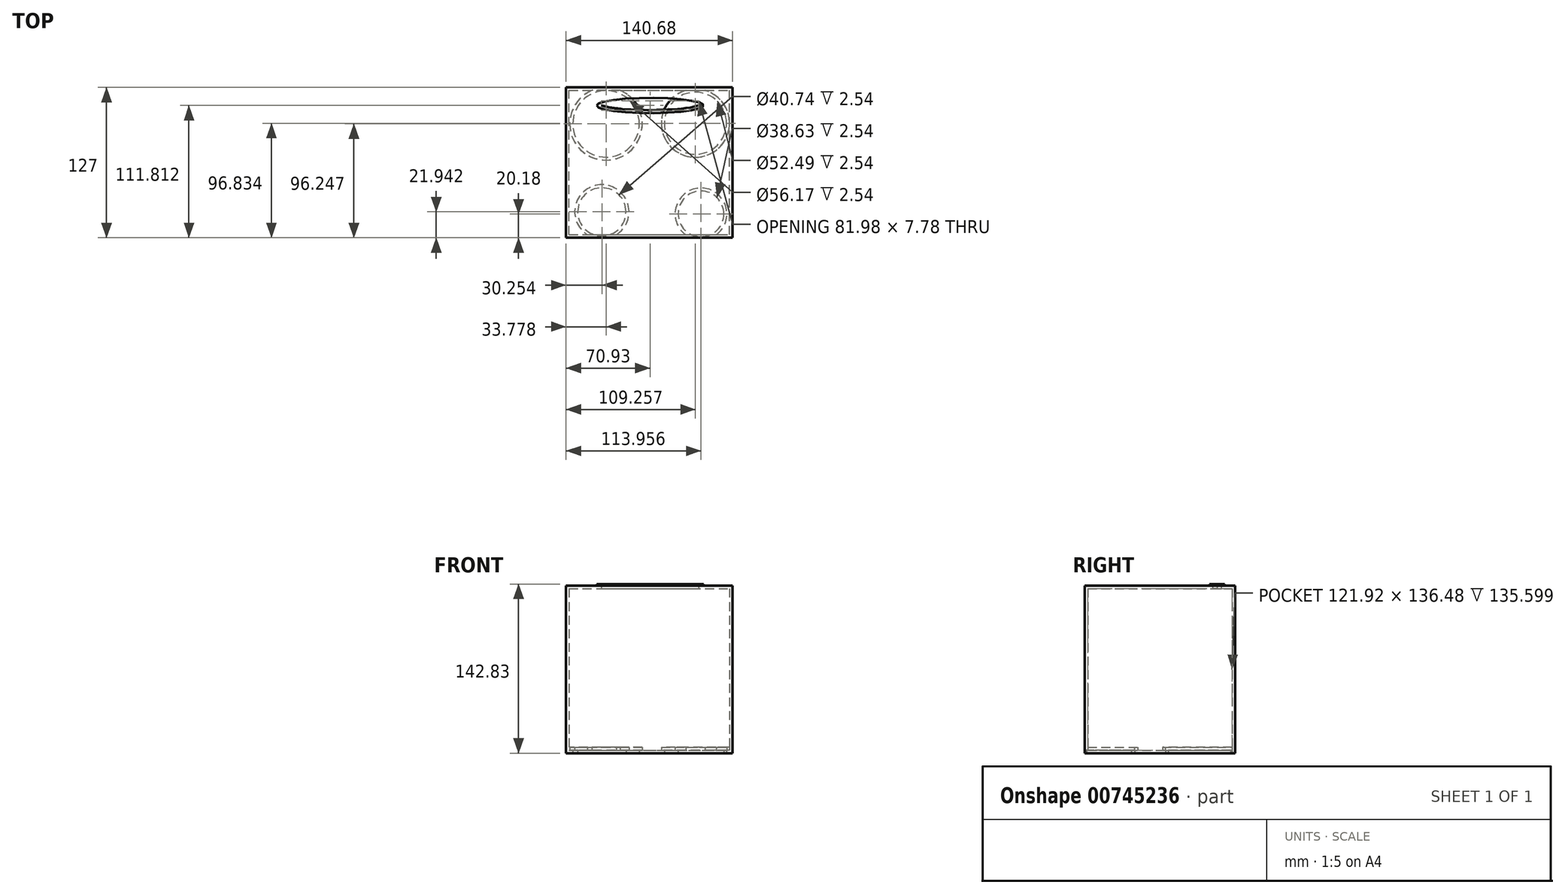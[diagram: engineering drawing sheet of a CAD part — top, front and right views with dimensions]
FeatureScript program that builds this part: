
annotation { "Feature Type Name" : "Feature", "Feature Type Description" : "" }
export const myFeature = defineFeature(function(context is Context, id is Id, definition is map)
    precondition{}
    {
        {
            var Q0;
            Q0=qCreatedBy(makeId("Front.planeOp"),FACE);
            var sketch = newSketch(context, id + "F0", { "sketchPlane" : qUnion([Q0])});
            skLineSegment(sketch, "E0.bottom", {"start": v(-70.93, 71.51) * mm, "end": v(69.75, 71.51) * mm});
            skLineSegment(sketch, "E0.top", {"start": v(-70.93, -70.05) * mm, "end": v(69.75, -70.05) * mm});
            skLineSegment(sketch, "E0.left", {"start": v(-70.93, 71.51) * mm, "end": v(-70.93, -70.05) * mm});
            skLineSegment(sketch, "E0.right", {"start": v(69.75, 71.51) * mm, "end": v(69.75, -70.05) * mm});
            skSolve(sketch);
        }
        {
            var Q0;
            Q0 = qSketchRegion(id + "F0", true);
            extrude(context, id + "F1", {"entities" : qUnion([Q0]), "depth" : 127 * mm, "offsetDistance" : 25.4 * mm});
        }
        {
            var Q0;
            Q0=makeQuery(id+"F1.opExtrude","SWEPT_FACE",FACE,{"disambiguationData":[OSD([sQuery(id+"F0.wireOp",EDGE,"E0.top")])]});
            var sketch = newSketch(context, id + "F2", { "sketchPlane" : qUnion([Q0])});
            skCircle(sketch, "E1", {"center": v(-40.68, 105.06) * mm, "radius": 20.37 * mm});
            skCircle(sketch, "E2", {"center": v(43.03, 106.82) * mm, "radius": 19.31 * mm});
            skCircle(sketch, "E3", {"center": v(38.33, 30.17) * mm, "radius": 26.24 * mm});
            skCircle(sketch, "E4", {"center": v(-37.15, 30.75) * mm, "radius": 28.09 * mm});
            skSolve(sketch);
        }
        {
            var Q0;
            Q0 = qSketchRegion(id + "F2", true);
            extrude(context, id + "F3", {"entities" : qUnion([Q0]), "operationType" : NewBodyOperationType.REMOVE, "oppositeDirection" : true, "depth" : 2.54 * mm, "offsetDistance" : 25.4 * mm});
        }
        {
            var Q0;
            Q0=makeQuery(id+"F1.opExtrude","SWEPT_FACE",FACE,{"disambiguationData":[OSD([sQuery(id+"F0.wireOp",EDGE,"E0.bottom")])]});
            var sketch = newSketch(context, id + "F4", { "sketchPlane" : qUnion([Q0])});
            skEllipse(sketch, "E5", {"center": v(0, -15.19) * mm, "majorRadius": 45.08 * mm, "minorRadius": 6.43 * mm, "majorAxis": v(-1, 0)});
            skSolve(sketch);
        }
        {
            var Q0;
            Q0 = qSketchRegion(id + "F4", true);
            extrude(context, id + "F5", {"entities" : qUnion([Q0]), "operationType" : NewBodyOperationType.ADD, "depth" : 1.27 * mm, "offsetDistance" : 25.4 * mm});
        }
        {
            var Q0;
            Q0=makeQuery(id+"F5.opExtrude","CAP_FACE",FACE,{"disambiguationData":[OSD([sQuery(id+"F4.wireOp",EDGE,"E5")])],"isStart":false});
            shell(context, id + "F6", {"entities" : qUnion([Q0]), "thickness" : 2.54 * mm});
        }
    });
